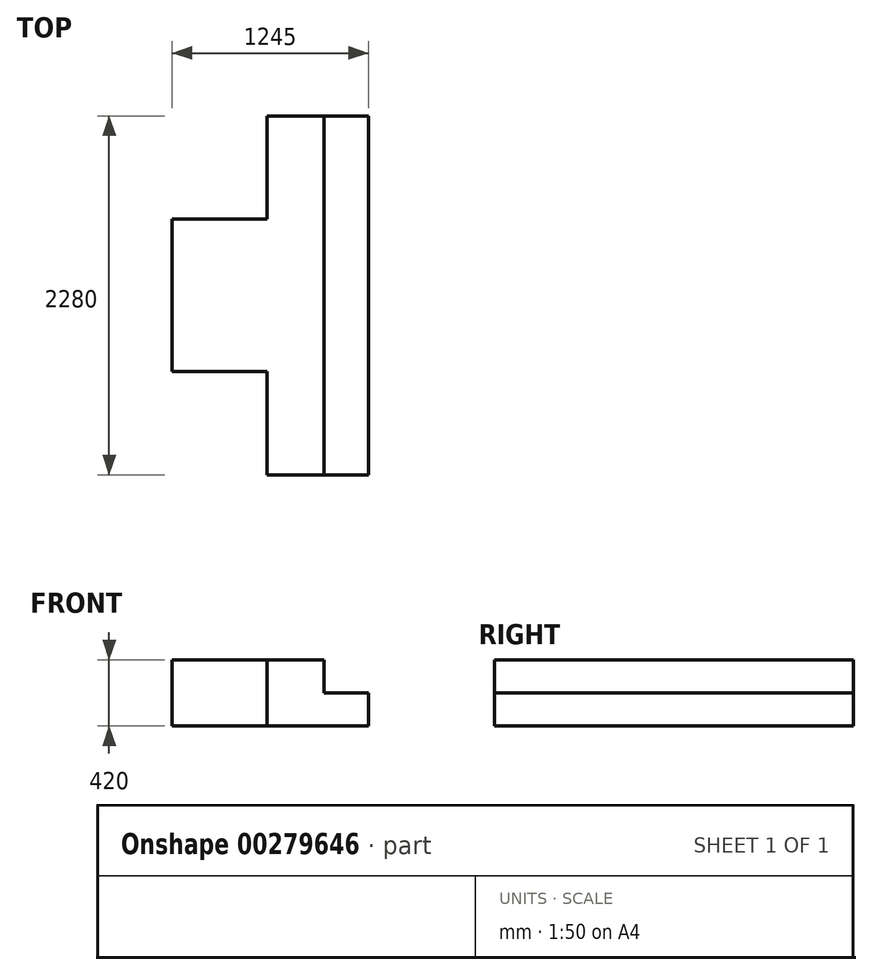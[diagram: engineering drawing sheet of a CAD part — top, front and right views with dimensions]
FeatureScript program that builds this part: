
annotation { "Feature Type Name" : "Feature", "Feature Type Description" : "" }
export const myFeature = defineFeature(function(context is Context, id is Id, definition is map)
    precondition{}
    {
        {
            var Q0;
            Q0=qCreatedBy(makeId("Front.planeOp"),FACE);
            var sketch = newSketch(context, id + "F0", { "sketchPlane" : qUnion([Q0])});
            skLineSegment(sketch, "E0", {"start": v(0, 0) * mm, "end": v(965, 0) * mm});
            skLineSegment(sketch, "E1", {"start": v(965, 0) * mm, "end": v(965, -210) * mm});
            skLineSegment(sketch, "E2", {"start": v(965, -210) * mm, "end": v(1245, -210) * mm});
            skLineSegment(sketch, "E3", {"start": v(1245, -210) * mm, "end": v(1245, -420) * mm});
            skLineSegment(sketch, "E4", {"start": v(0, 0) * mm, "end": v(0, -420) * mm});
            skLineSegment(sketch, "E5", {"start": v(0, -420) * mm, "end": v(1245, -420) * mm});
            skSolve(sketch);
        }
        {
            var Q0;
            Q0=makeQuery(id+"F0.imprint","IMPRINT",FACE,{"disambiguationData":[TD([[makeQuery(id+"F0.imprint","IMPRINT",EDGE,{"derivedFrom":sQuery(id+"F0.wireOp",EDGE,"E0")}),-1.0]])]});
            extrude(context, id + "F1", {"entities" : qUnion([Q0]), "endBound" : BoundingType.SYMMETRIC, "depth" : 2280 * mm});
        }
        {
            var Q0;
            Q0=makeQuery(id+"F1.opExtrude","CAP_FACE",FACE,{"disambiguationData":[OSD([sQuery(id+"F0.wireOp",EDGE,"E0"),sQuery(id+"F0.wireOp",EDGE,"E1"),sQuery(id+"F0.wireOp",EDGE,"E2"),sQuery(id+"F0.wireOp",EDGE,"E3"),sQuery(id+"F0.wireOp",EDGE,"E4"),sQuery(id+"F0.wireOp",EDGE,"E5")])],"isStart":false});
            var sketch = newSketch(context, id + "F2", { "sketchPlane" : qUnion([Q0])});
            skLineSegment(sketch, "E6.bottom", {"start": v(0, 0) * mm, "end": v(600, 0) * mm});
            skLineSegment(sketch, "E6.top", {"start": v(0, -420) * mm, "end": v(600, -420) * mm});
            skLineSegment(sketch, "E6.left", {"start": v(0, 0) * mm, "end": v(0, -420) * mm});
            skLineSegment(sketch, "E6.right", {"start": v(600, 0) * mm, "end": v(600, -420) * mm});
            skSolve(sketch);
        }
        {
            var Q0;
            Q0=makeQuery(id+"F2.imprint","IMPRINT",FACE,{"disambiguationData":[TD([[makeQuery(id+"F2.imprint","IMPRINT",EDGE,{"derivedFrom":sQuery(id+"F2.wireOp",EDGE,"E6.bottom")}),-1.0]])]});
            extrude(context, id + "F3", {"entities" : qUnion([Q0]), "operationType" : NewBodyOperationType.REMOVE, "oppositeDirection" : true, "depth" : 655 * mm});
        }
        {
            var Q0;
            Q0=makeQuery(id+"F1.opExtrude","CAP_FACE",FACE,{"disambiguationData":[OSD([sQuery(id+"F0.wireOp",EDGE,"E0"),sQuery(id+"F0.wireOp",EDGE,"E1"),sQuery(id+"F0.wireOp",EDGE,"E2"),sQuery(id+"F0.wireOp",EDGE,"E3"),sQuery(id+"F0.wireOp",EDGE,"E4"),sQuery(id+"F0.wireOp",EDGE,"E5")])],"isStart":true});
            var sketch = newSketch(context, id + "F4", { "sketchPlane" : qUnion([Q0])});
            skLineSegment(sketch, "E7.bottom", {"start": v(0, 0) * mm, "end": v(-600, 0) * mm});
            skLineSegment(sketch, "E7.top", {"start": v(0, -420) * mm, "end": v(-600, -420) * mm});
            skLineSegment(sketch, "E7.left", {"start": v(0, 0) * mm, "end": v(0, -420) * mm});
            skLineSegment(sketch, "E7.right", {"start": v(-600, 0) * mm, "end": v(-600, -420) * mm});
            skSolve(sketch);
        }
        {
            var Q0;
            Q0=makeQuery(id+"F4.imprint","IMPRINT",FACE,{"disambiguationData":[TD([[makeQuery(id+"F4.imprint","IMPRINT",EDGE,{"derivedFrom":sQuery(id+"F4.wireOp",EDGE,"E7.bottom")}),1.0]])]});
            extrude(context, id + "F5", {"entities" : qUnion([Q0]), "operationType" : NewBodyOperationType.REMOVE, "oppositeDirection" : true, "depth" : 655 * mm});
        }
    });
